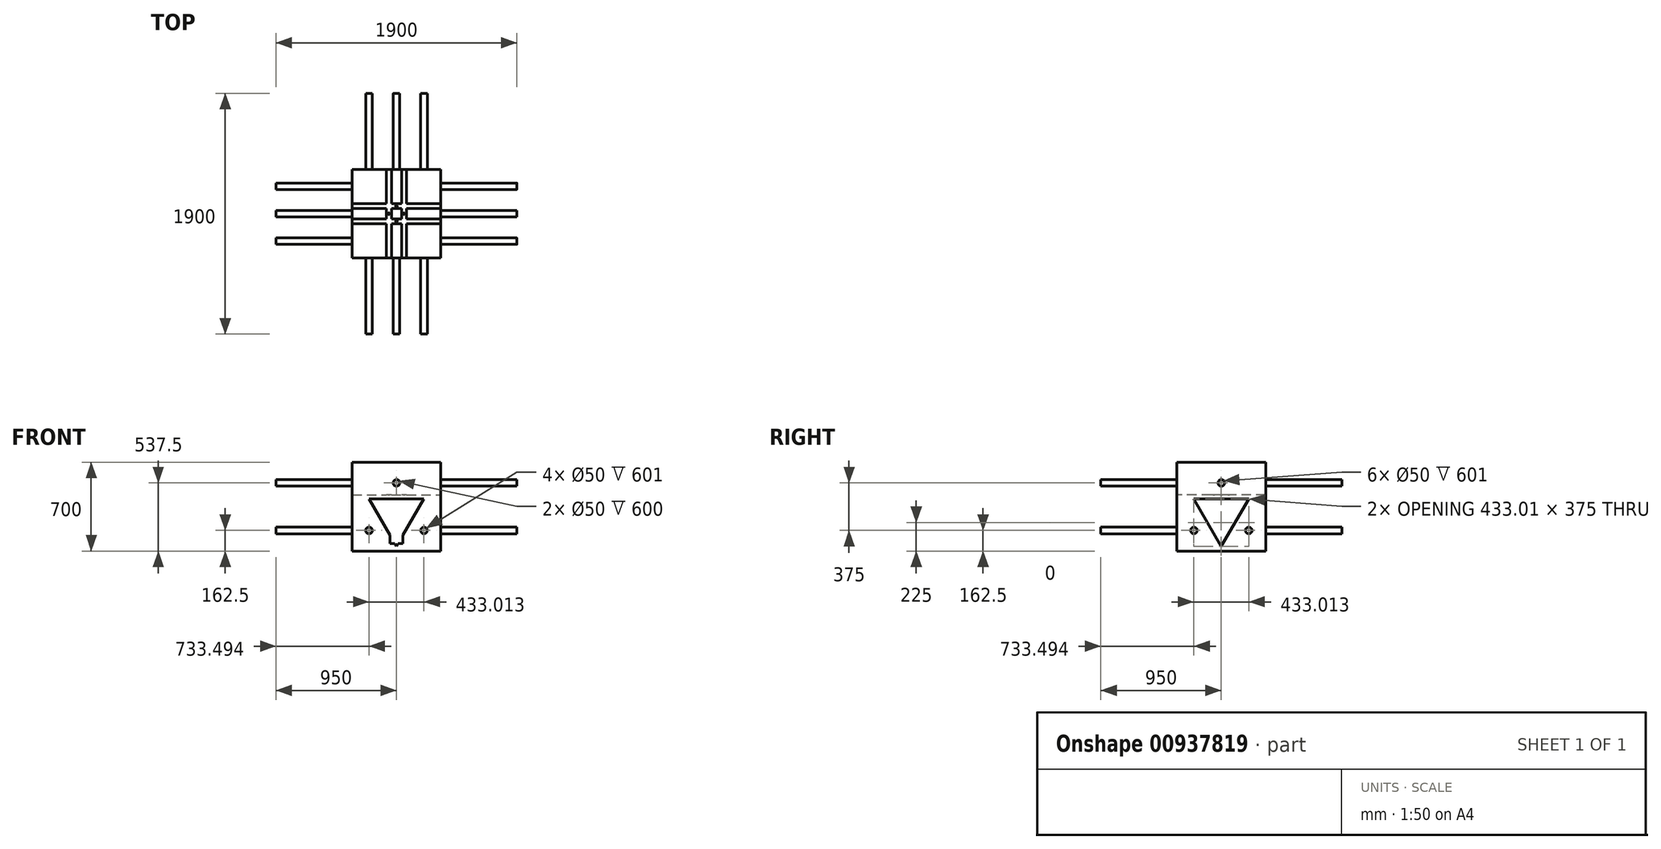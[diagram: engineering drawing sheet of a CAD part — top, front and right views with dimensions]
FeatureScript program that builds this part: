
annotation { "Feature Type Name" : "Feature", "Feature Type Description" : "" }
export const myFeature = defineFeature(function(context is Context, id is Id, definition is map)
    precondition{}
    {
        {
            var Q0;
            Q0=qCreatedBy(makeId("Top.planeOp"),FACE);
            var sketch = newSketch(context, id + "F0", { "sketchPlane" : qUnion([Q0])});
            skLineSegment(sketch, "E0.bottom", {"start": v(350, 350) * mm, "end": v(-350, 350) * mm});
            skLineSegment(sketch, "E0.top", {"start": v(350, -350) * mm, "end": v(-350, -350) * mm});
            skLineSegment(sketch, "E0.left", {"start": v(350, 350) * mm, "end": v(350, -350) * mm});
            skLineSegment(sketch, "E0.right", {"start": v(-350, 350) * mm, "end": v(-350, -350) * mm});
            skPoint(sketch, "E0.middle", {"position": v(0, 0) * mm});
            skLineSegment(sketch, "E1.bottom", {"start": v(349, 349) * mm, "end": v(-349, 349) * mm});
            skLineSegment(sketch, "E1.top", {"start": v(349, -349) * mm, "end": v(-349, -349) * mm});
            skLineSegment(sketch, "E1.left", {"start": v(349, 349) * mm, "end": v(349, -349) * mm});
            skLineSegment(sketch, "E1.right", {"start": v(-349, 349) * mm, "end": v(-349, -349) * mm});
            skLineSegment(sketch, "E2.bottom", {"start": v(-70, 70) * mm, "end": v(70, 70) * mm});
            skLineSegment(sketch, "E2.top", {"start": v(-70, -70) * mm, "end": v(70, -70) * mm});
            skLineSegment(sketch, "E2.left", {"start": v(-70, 70) * mm, "end": v(-70, -70) * mm});
            skLineSegment(sketch, "E2.right", {"start": v(70, 70) * mm, "end": v(70, -70) * mm});
            skSolve(sketch);
        }
        {
            var Q0;
            Q0=makeQuery(id+"F0.imprint","IMPRINT",FACE,{"disambiguationData":[TD([[makeQuery(id+"F0.imprint","IMPRINT",EDGE,{"derivedFrom":sQuery(id+"F0.wireOp",EDGE,"E0.bottom")}),1.0]])]});
            extrude(context, id + "F1", {"entities" : qUnion([Q0]), "oppositeDirection" : true, "depth" : 700 * mm, "offsetDistance" : 25 * mm});
        }
        {
            var Q0;
            Q0=makeQuery(id+"F1.opExtrude","SWEPT_FACE",FACE,{"disambiguationData":[OSD([sQuery(id+"F0.wireOp",EDGE,"E0.left")])]});
            var sketch = newSketch(context, id + "F2", { "sketchPlane" : qUnion([Q0])});
            skPoint(sketch, "E3", {"position": v(0, -350) * mm});
            skPoint(sketch, "E3.positionSnap0", {"position": v(-350, -350) * mm});
            skPoint(sketch, "E3.positionSnap1", {"position": v(0, 0) * mm});
            skCircle(sketch, "E4.cCircle", {"center": v(0, -412.5) * mm, "radius": 250 * mm, "construction": true});
            skLineSegment(sketch, "E4.0", {"start": v(0, -162.5) * mm, "end": v(216.5, -537.5) * mm});
            skLineSegment(sketch, "E4.1", {"start": v(216.5, -537.5) * mm, "end": v(-216.5, -537.5) * mm});
            skLineSegment(sketch, "E4.2", {"start": v(-216.5, -537.5) * mm, "end": v(0, -162.5) * mm});
            skCircle(sketch, "E5", {"center": v(0, -162.5) * mm, "radius": 25 * mm});
            skCircle(sketch, "E6", {"center": v(216.5, -537.5) * mm, "radius": 25 * mm});
            skCircle(sketch, "E7", {"center": v(-216.5, -537.5) * mm, "radius": 25 * mm});
            skCircle(sketch, "E8", {"center": v(0, -162.5) * mm, "radius": 26 * mm});
            skCircle(sketch, "E9", {"center": v(-216.5, -537.5) * mm, "radius": 26 * mm});
            skCircle(sketch, "E10", {"center": v(216.5, -537.5) * mm, "radius": 26 * mm});
            skPoint(sketch, "E11", {"position": v(-350, -175) * mm});
            skPoint(sketch, "E12", {"position": v(350, -175) * mm});
            skLineSegment(sketch, "E13", {"start": v(0, 0) * mm, "end": v(349, -175) * mm});
            skLineSegment(sketch, "E14", {"start": v(349, -175) * mm, "end": v(349, 0) * mm});
            skLineSegment(sketch, "E15", {"start": v(0, 0) * mm, "end": v(-349, -175) * mm});
            skLineSegment(sketch, "E16", {"start": v(-349, -175) * mm, "end": v(-349, 0) * mm});
            skPoint(sketch, "E17.cCircle.perimeterSnap0", {"position": v(0, -537.5) * mm});
            skPoint(sketch, "E17.0.startSnap0", {"position": v(0, -537.5) * mm});
            skLineSegment(sketch, "E18.0", {"start": v(0, -662.5) * mm, "end": v(-216.5, -287.5) * mm});
            skLineSegment(sketch, "E18.1", {"start": v(-216.5, -287.5) * mm, "end": v(216.5, -287.5) * mm});
            skLineSegment(sketch, "E18.2", {"start": v(216.5, -287.5) * mm, "end": v(0, -662.5) * mm});
            skLineSegment(sketch, "E19", {"start": v(-350, -256.5) * mm, "end": v(350, -256.5) * mm});
            skLineSegment(sketch, "E20", {"start": v(-350, -257.5) * mm, "end": v(350, -257.5) * mm});
            skPoint(sketch, "E21", {"position": v(0, -256.5) * mm});
            skPoint(sketch, "E22", {"position": v(0, -257.5) * mm});
            skPoint(sketch, "E23", {"position": v(-80, -256.5) * mm});
            skPoint(sketch, "E24", {"position": v(-80, -257.5) * mm});
            skPoint(sketch, "E25", {"position": v(80, -256.5) * mm});
            skPoint(sketch, "E26", {"position": v(80, -257.5) * mm});
            skLineSegment(sketch, "E27", {"start": v(-80, -256.5) * mm, "end": v(-80, -257.5) * mm});
            skLineSegment(sketch, "E28", {"start": v(80, -256.5) * mm, "end": v(80, -257.5) * mm});
            skPoint(sketch, "E29", {"position": v(-40, -256.5) * mm});
            skPoint(sketch, "E30", {"position": v(-40, -257.5) * mm});
            skPoint(sketch, "E31", {"position": v(40, -256.5) * mm});
            skPoint(sketch, "E32", {"position": v(40, -257.5) * mm});
            skLineSegment(sketch, "E33", {"start": v(-40, -256.5) * mm, "end": v(-40, -257.5) * mm});
            skLineSegment(sketch, "E34", {"start": v(40, -256.5) * mm, "end": v(40, -257.5) * mm});
            skSolve(sketch);
        }
        {
            var Q0;
            Q0=makeQuery(id+"F1.opExtrude","SWEPT_FACE",FACE,{"disambiguationData":[OSD([sQuery(id+"F0.wireOp",EDGE,"E0.top")])]});
            var sketch = newSketch(context, id + "F3", { "sketchPlane" : qUnion([Q0])});
            skPoint(sketch, "E35", {"position": v(0, -412.5) * mm});
            skPoint(sketch, "E35.positionSnap1", {"position": v(0, 157.53) * mm});
            skCircle(sketch, "E36.cCircle", {"center": v(0, -412.5) * mm, "radius": 250 * mm, "construction": true});
            skLineSegment(sketch, "E36.0", {"start": v(0, -162.5) * mm, "end": v(216.5, -537.5) * mm});
            skLineSegment(sketch, "E36.1", {"start": v(216.5, -537.5) * mm, "end": v(-216.5, -537.5) * mm});
            skLineSegment(sketch, "E36.2", {"start": v(-216.5, -537.5) * mm, "end": v(0, -162.5) * mm});
            skCircle(sketch, "E37", {"center": v(0, -162.5) * mm, "radius": 25 * mm});
            skCircle(sketch, "E38", {"center": v(216.5, -537.5) * mm, "radius": 25 * mm});
            skCircle(sketch, "E39", {"center": v(-216.5, -537.5) * mm, "radius": 25 * mm});
            skCircle(sketch, "E40", {"center": v(0, -162.5) * mm, "radius": 26 * mm});
            skCircle(sketch, "E41", {"center": v(-216.5, -537.5) * mm, "radius": 26 * mm});
            skCircle(sketch, "E42", {"center": v(216.5, -537.5) * mm, "radius": 26 * mm});
            skPoint(sketch, "E43", {"position": v(-350, -350) * mm});
            skPoint(sketch, "E44", {"position": v(-350, -175) * mm});
            skPoint(sketch, "E45", {"position": v(350, -175) * mm});
            skLineSegment(sketch, "E46", {"start": v(0, 0) * mm, "end": v(-349, -175) * mm});
            skLineSegment(sketch, "E47", {"start": v(-349, -175) * mm, "end": v(-349, 0) * mm});
            skLineSegment(sketch, "E48", {"start": v(0, 0) * mm, "end": v(349, -175) * mm});
            skLineSegment(sketch, "E49", {"start": v(349, -175) * mm, "end": v(349, 0) * mm});
            skLineSegment(sketch, "E50.0", {"start": v(0, -662.5) * mm, "end": v(-216.5, -287.5) * mm});
            skLineSegment(sketch, "E50.1", {"start": v(-216.5, -287.5) * mm, "end": v(216.5, -287.5) * mm});
            skLineSegment(sketch, "E50.2", {"start": v(216.5, -287.5) * mm, "end": v(0, -662.5) * mm});
            skPoint(sketch, "E51", {"position": v(-350, -257.5) * mm});
            skPoint(sketch, "E52", {"position": v(-350, -256.5) * mm});
            skPoint(sketch, "E53", {"position": v(350, -256.5) * mm});
            skPoint(sketch, "E54", {"position": v(350, -257.5) * mm});
            skLineSegment(sketch, "E55", {"start": v(-350, -256.5) * mm, "end": v(350, -256.5) * mm});
            skLineSegment(sketch, "E56", {"start": v(-350, -257.5) * mm, "end": v(350, -257.5) * mm});
            skPoint(sketch, "E57", {"position": v(0, -257.5) * mm});
            skPoint(sketch, "E58", {"position": v(0, -256.5) * mm});
            skPoint(sketch, "E59", {"position": v(-80, -256.5) * mm});
            skPoint(sketch, "E60", {"position": v(-80, -257.5) * mm});
            skPoint(sketch, "E61", {"position": v(80, -256.5) * mm});
            skPoint(sketch, "E62", {"position": v(80, -257.5) * mm});
            skPoint(sketch, "E63", {"position": v(-40, -256.5) * mm});
            skPoint(sketch, "E64", {"position": v(-40, -257.5) * mm});
            skPoint(sketch, "E65", {"position": v(40, -256.5) * mm});
            skPoint(sketch, "E66", {"position": v(40, -257.5) * mm});
            skLineSegment(sketch, "E67", {"start": v(-80, -256.5) * mm, "end": v(-80, -257.5) * mm});
            skLineSegment(sketch, "E68", {"start": v(-40, -256.5) * mm, "end": v(-40, -257.5) * mm});
            skLineSegment(sketch, "E69", {"start": v(40, -256.5) * mm, "end": v(40, -257.5) * mm});
            skLineSegment(sketch, "E70", {"start": v(80, -257.5) * mm, "end": v(80, -256.5) * mm});
            skSolve(sketch);
        }
        {
            var Q0;
            Q0=makeQuery(id+"F1.opExtrude","SWEPT_FACE",FACE,{"disambiguationData":[OSD([sQuery(id+"F0.wireOp",EDGE,"E0.right")])]});
            var sketch = newSketch(context, id + "F4", { "sketchPlane" : qUnion([Q0])});
            skPoint(sketch, "E71", {"position": v(0, -350) * mm});
            skPoint(sketch, "E71.positionSnap0", {"position": v(-350, -350) * mm});
            skPoint(sketch, "E71.positionSnap1", {"position": v(0, 0) * mm});
            skCircle(sketch, "E72.cCircle", {"center": v(0, -412.5) * mm, "radius": 250 * mm, "construction": true});
            skLineSegment(sketch, "E72.0", {"start": v(0, -162.5) * mm, "end": v(216.5, -537.5) * mm});
            skLineSegment(sketch, "E72.1", {"start": v(216.5, -537.5) * mm, "end": v(-216.5, -537.5) * mm});
            skLineSegment(sketch, "E72.2", {"start": v(-216.5, -537.5) * mm, "end": v(0, -162.5) * mm});
            skCircle(sketch, "E73", {"center": v(0, -162.5) * mm, "radius": 25 * mm});
            skCircle(sketch, "E74", {"center": v(216.5, -537.5) * mm, "radius": 25 * mm});
            skCircle(sketch, "E75", {"center": v(-216.5, -537.5) * mm, "radius": 25 * mm});
            skCircle(sketch, "E76", {"center": v(0, -162.5) * mm, "radius": 26 * mm});
            skCircle(sketch, "E77", {"center": v(-216.5, -537.5) * mm, "radius": 26 * mm});
            skCircle(sketch, "E78", {"center": v(216.5, -537.5) * mm, "radius": 26 * mm});
            skSolve(sketch);
        }
        {
            var Q0;
            Q0=makeQuery(id+"F1.opExtrude","SWEPT_FACE",FACE,{"disambiguationData":[OSD([sQuery(id+"F0.wireOp",EDGE,"E0.bottom")])]});
            var sketch = newSketch(context, id + "F5", { "sketchPlane" : qUnion([Q0])});
            skPoint(sketch, "E79", {"position": v(0, -350) * mm});
            skPoint(sketch, "E79.positionSnap0", {"position": v(-350, -350) * mm});
            skPoint(sketch, "E79.positionSnap1", {"position": v(0, 0) * mm});
            skCircle(sketch, "E80.cCircle", {"center": v(0, -412.5) * mm, "radius": 250 * mm, "construction": true});
            skLineSegment(sketch, "E80.0", {"start": v(0, -162.5) * mm, "end": v(216.5, -537.5) * mm});
            skLineSegment(sketch, "E80.1", {"start": v(216.5, -537.5) * mm, "end": v(-216.5, -537.5) * mm});
            skLineSegment(sketch, "E80.2", {"start": v(-216.5, -537.5) * mm, "end": v(0, -162.5) * mm});
            skCircle(sketch, "E81", {"center": v(0, -162.5) * mm, "radius": 25 * mm});
            skCircle(sketch, "E82", {"center": v(216.5, -537.5) * mm, "radius": 25 * mm});
            skCircle(sketch, "E83", {"center": v(-216.5, -537.5) * mm, "radius": 25 * mm});
            skCircle(sketch, "E84", {"center": v(0, -162.5) * mm, "radius": 26 * mm});
            skCircle(sketch, "E85", {"center": v(216.5, -537.5) * mm, "radius": 26 * mm});
            skCircle(sketch, "E86", {"center": v(-216.5, -537.5) * mm, "radius": 26 * mm});
            skSolve(sketch);
        }
        {
            var Q0;
            {var subQ0=sQuery(id+"F2.wireOp",EDGE,"E5");var subQ1=sQuery(id+"F2.wireOp",EDGE,"E4.0");var subQ2=makeQuery(id+"F2.imprint","INTERSECT",VERTEX,{"derivedFrom":[subQ1,subQ0]});Q0=makeQuery(id+"F2.imprint","IMPRINT",FACE,{"disambiguationData":[TD([[makeQuery(id+"F2.imprint","IMPRINT",EDGE,{"disambiguationData":[TD([[subQ2,-1.0]])],"derivedFrom":subQ1}),1.0]])]});}
            var Q1;
            {var subQ0=sQuery(id+"F2.wireOp",EDGE,"E10");var subQ1=sQuery(id+"F2.wireOp",EDGE,"E4.0");var subQ2=makeQuery(id+"F2.imprint","INTERSECT",VERTEX,{"derivedFrom":[subQ1,subQ0]});Q1=makeQuery(id+"F2.imprint","IMPRINT",FACE,{"disambiguationData":[TD([[makeQuery(id+"F2.imprint","IMPRINT",EDGE,{"disambiguationData":[TD([[subQ2,-1.0]])],"derivedFrom":subQ1}),1.0]])]});}
            var Q2;
            {var subQ0=sQuery(id+"F2.wireOp",EDGE,"E10");var subQ1=sQuery(id+"F2.wireOp",EDGE,"E4.0");var subQ2=makeQuery(id+"F2.imprint","INTERSECT",VERTEX,{"derivedFrom":[subQ1,subQ0]});Q2=makeQuery(id+"F2.imprint","IMPRINT",FACE,{"disambiguationData":[TD([[makeQuery(id+"F2.imprint","IMPRINT",EDGE,{"disambiguationData":[TD([[subQ2,-1.0]])],"derivedFrom":subQ1}),-1.0]])]});}
            var Q3;
            {var subQ0=sQuery(id+"F2.wireOp",EDGE,"E5");var subQ1=sQuery(id+"F2.wireOp",EDGE,"E4.0");var subQ2=makeQuery(id+"F2.imprint","INTERSECT",VERTEX,{"derivedFrom":[subQ1,subQ0]});Q3=makeQuery(id+"F2.imprint","IMPRINT",FACE,{"disambiguationData":[TD([[makeQuery(id+"F2.imprint","IMPRINT",EDGE,{"disambiguationData":[TD([[subQ2,-1.0]])],"derivedFrom":subQ1}),-1.0]])]});}
            var Q4;
            {var subQ0=sQuery(id+"F2.wireOp",EDGE,"E9");var subQ1=sQuery(id+"F2.wireOp",EDGE,"E4.1");var subQ2=makeQuery(id+"F2.imprint","INTERSECT",VERTEX,{"derivedFrom":[subQ1,subQ0]});Q4=makeQuery(id+"F2.imprint","IMPRINT",FACE,{"disambiguationData":[TD([[makeQuery(id+"F2.imprint","IMPRINT",EDGE,{"disambiguationData":[TD([[subQ2,-1.0]])],"derivedFrom":subQ1}),1.0]])]});}
            var Q5;
            {var subQ0=sQuery(id+"F2.wireOp",EDGE,"E9");var subQ1=sQuery(id+"F2.wireOp",EDGE,"E4.1");var subQ2=makeQuery(id+"F2.imprint","INTERSECT",VERTEX,{"derivedFrom":[subQ1,subQ0]});Q5=makeQuery(id+"F2.imprint","IMPRINT",FACE,{"disambiguationData":[TD([[makeQuery(id+"F2.imprint","IMPRINT",EDGE,{"disambiguationData":[TD([[subQ2,-1.0]])],"derivedFrom":subQ1}),-1.0]])]});}
            extrude(context, id + "F6", {"entities" : qUnion([Q0, Q1, Q2, Q3, Q4, Q5]), "operationType" : NewBodyOperationType.ADD, "depth" : 600 * mm, "offsetDistance" : 25 * mm});
        }
        {
            var Q0;
            {var subQ0=sQuery(id+"F3.wireOp",EDGE,"E37");var subQ1=sQuery(id+"F3.wireOp",EDGE,"E36.0");var subQ2=makeQuery(id+"F3.imprint","INTERSECT",VERTEX,{"derivedFrom":[subQ1,subQ0]});Q0=makeQuery(id+"F3.imprint","IMPRINT",FACE,{"disambiguationData":[TD([[makeQuery(id+"F3.imprint","IMPRINT",EDGE,{"disambiguationData":[TD([[subQ2,-1.0]])],"derivedFrom":subQ1}),-1.0]])]});}
            var Q1;
            {var subQ0=sQuery(id+"F3.wireOp",EDGE,"E37");var subQ1=sQuery(id+"F3.wireOp",EDGE,"E36.0");var subQ2=makeQuery(id+"F3.imprint","INTERSECT",VERTEX,{"derivedFrom":[subQ1,subQ0]});Q1=makeQuery(id+"F3.imprint","IMPRINT",FACE,{"disambiguationData":[TD([[makeQuery(id+"F3.imprint","IMPRINT",EDGE,{"disambiguationData":[TD([[subQ2,-1.0]])],"derivedFrom":subQ1}),1.0]])]});}
            var Q2;
            {var subQ0=sQuery(id+"F3.wireOp",EDGE,"E41");var subQ1=sQuery(id+"F3.wireOp",EDGE,"E36.1");var subQ2=makeQuery(id+"F3.imprint","INTERSECT",VERTEX,{"derivedFrom":[subQ1,subQ0]});Q2=makeQuery(id+"F3.imprint","IMPRINT",FACE,{"disambiguationData":[TD([[makeQuery(id+"F3.imprint","IMPRINT",EDGE,{"disambiguationData":[TD([[subQ2,-1.0]])],"derivedFrom":subQ1}),1.0]])]});}
            var Q3;
            {var subQ0=sQuery(id+"F3.wireOp",EDGE,"E41");var subQ1=sQuery(id+"F3.wireOp",EDGE,"E36.1");var subQ2=makeQuery(id+"F3.imprint","INTERSECT",VERTEX,{"derivedFrom":[subQ1,subQ0]});Q3=makeQuery(id+"F3.imprint","IMPRINT",FACE,{"disambiguationData":[TD([[makeQuery(id+"F3.imprint","IMPRINT",EDGE,{"disambiguationData":[TD([[subQ2,-1.0]])],"derivedFrom":subQ1}),-1.0]])]});}
            var Q4;
            {var subQ0=sQuery(id+"F3.wireOp",EDGE,"E42");var subQ1=sQuery(id+"F3.wireOp",EDGE,"E36.0");var subQ2=makeQuery(id+"F3.imprint","INTERSECT",VERTEX,{"derivedFrom":[subQ1,subQ0]});Q4=makeQuery(id+"F3.imprint","IMPRINT",FACE,{"disambiguationData":[TD([[makeQuery(id+"F3.imprint","IMPRINT",EDGE,{"disambiguationData":[TD([[subQ2,-1.0]])],"derivedFrom":subQ1}),1.0]])]});}
            var Q5;
            {var subQ0=sQuery(id+"F3.wireOp",EDGE,"E42");var subQ1=sQuery(id+"F3.wireOp",EDGE,"E36.0");var subQ2=makeQuery(id+"F3.imprint","INTERSECT",VERTEX,{"derivedFrom":[subQ1,subQ0]});Q5=makeQuery(id+"F3.imprint","IMPRINT",FACE,{"disambiguationData":[TD([[makeQuery(id+"F3.imprint","IMPRINT",EDGE,{"disambiguationData":[TD([[subQ2,-1.0]])],"derivedFrom":subQ1}),-1.0]])]});}
            extrude(context, id + "F7", {"entities" : qUnion([Q0, Q1, Q2, Q3, Q4, Q5]), "operationType" : NewBodyOperationType.ADD, "depth" : 600 * mm, "offsetDistance" : 25 * mm});
        }
        {
            var Q0;
            {var subQ0=sQuery(id+"F4.wireOp",EDGE,"E73");var subQ1=sQuery(id+"F4.wireOp",EDGE,"E72.0");var subQ2=makeQuery(id+"F4.imprint","INTERSECT",VERTEX,{"derivedFrom":[subQ1,subQ0]});Q0=makeQuery(id+"F4.imprint","IMPRINT",FACE,{"disambiguationData":[TD([[makeQuery(id+"F4.imprint","IMPRINT",EDGE,{"disambiguationData":[TD([[subQ2,-1.0]])],"derivedFrom":subQ1}),1.0]])]});}
            var Q1;
            {var subQ0=sQuery(id+"F4.wireOp",EDGE,"E73");var subQ1=sQuery(id+"F4.wireOp",EDGE,"E72.0");var subQ2=makeQuery(id+"F4.imprint","INTERSECT",VERTEX,{"derivedFrom":[subQ1,subQ0]});Q1=makeQuery(id+"F4.imprint","IMPRINT",FACE,{"disambiguationData":[TD([[makeQuery(id+"F4.imprint","IMPRINT",EDGE,{"disambiguationData":[TD([[subQ2,-1.0]])],"derivedFrom":subQ1}),-1.0]])]});}
            var Q2;
            {var subQ0=sQuery(id+"F4.wireOp",EDGE,"E78");var subQ1=sQuery(id+"F4.wireOp",EDGE,"E72.0");var subQ2=makeQuery(id+"F4.imprint","INTERSECT",VERTEX,{"derivedFrom":[subQ1,subQ0]});Q2=makeQuery(id+"F4.imprint","IMPRINT",FACE,{"disambiguationData":[TD([[makeQuery(id+"F4.imprint","IMPRINT",EDGE,{"disambiguationData":[TD([[subQ2,-1.0]])],"derivedFrom":subQ1}),1.0]])]});}
            var Q3;
            {var subQ0=sQuery(id+"F4.wireOp",EDGE,"E78");var subQ1=sQuery(id+"F4.wireOp",EDGE,"E72.0");var subQ2=makeQuery(id+"F4.imprint","INTERSECT",VERTEX,{"derivedFrom":[subQ1,subQ0]});Q3=makeQuery(id+"F4.imprint","IMPRINT",FACE,{"disambiguationData":[TD([[makeQuery(id+"F4.imprint","IMPRINT",EDGE,{"disambiguationData":[TD([[subQ2,-1.0]])],"derivedFrom":subQ1}),-1.0]])]});}
            var Q4;
            {var subQ0=sQuery(id+"F4.wireOp",EDGE,"E77");var subQ1=sQuery(id+"F4.wireOp",EDGE,"E72.1");var subQ2=makeQuery(id+"F4.imprint","INTERSECT",VERTEX,{"derivedFrom":[subQ1,subQ0]});Q4=makeQuery(id+"F4.imprint","IMPRINT",FACE,{"disambiguationData":[TD([[makeQuery(id+"F4.imprint","IMPRINT",EDGE,{"disambiguationData":[TD([[subQ2,-1.0]])],"derivedFrom":subQ1}),1.0]])]});}
            var Q5;
            {var subQ0=sQuery(id+"F4.wireOp",EDGE,"E77");var subQ1=sQuery(id+"F4.wireOp",EDGE,"E72.1");var subQ2=makeQuery(id+"F4.imprint","INTERSECT",VERTEX,{"derivedFrom":[subQ1,subQ0]});Q5=makeQuery(id+"F4.imprint","IMPRINT",FACE,{"disambiguationData":[TD([[makeQuery(id+"F4.imprint","IMPRINT",EDGE,{"disambiguationData":[TD([[subQ2,-1.0]])],"derivedFrom":subQ1}),-1.0]])]});}
            extrude(context, id + "F8", {"entities" : qUnion([Q0, Q1, Q2, Q3, Q4, Q5]), "operationType" : NewBodyOperationType.ADD, "depth" : 600 * mm, "offsetDistance" : 25 * mm});
        }
        {
            var Q0;
            {var subQ0=sQuery(id+"F5.wireOp",EDGE,"E81");var subQ1=sQuery(id+"F5.wireOp",EDGE,"E80.0");var subQ2=makeQuery(id+"F5.imprint","INTERSECT",VERTEX,{"derivedFrom":[subQ1,subQ0]});Q0=makeQuery(id+"F5.imprint","IMPRINT",FACE,{"disambiguationData":[TD([[makeQuery(id+"F5.imprint","IMPRINT",EDGE,{"disambiguationData":[TD([[subQ2,-1.0]])],"derivedFrom":subQ1}),-1.0]])]});}
            var Q1;
            {var subQ0=sQuery(id+"F5.wireOp",EDGE,"E81");var subQ1=sQuery(id+"F5.wireOp",EDGE,"E80.0");var subQ2=makeQuery(id+"F5.imprint","INTERSECT",VERTEX,{"derivedFrom":[subQ1,subQ0]});Q1=makeQuery(id+"F5.imprint","IMPRINT",FACE,{"disambiguationData":[TD([[makeQuery(id+"F5.imprint","IMPRINT",EDGE,{"disambiguationData":[TD([[subQ2,-1.0]])],"derivedFrom":subQ1}),1.0]])]});}
            var Q2;
            {var subQ0=sQuery(id+"F5.wireOp",EDGE,"E86");var subQ1=sQuery(id+"F5.wireOp",EDGE,"E80.1");var subQ2=makeQuery(id+"F5.imprint","INTERSECT",VERTEX,{"derivedFrom":[subQ1,subQ0]});Q2=makeQuery(id+"F5.imprint","IMPRINT",FACE,{"disambiguationData":[TD([[makeQuery(id+"F5.imprint","IMPRINT",EDGE,{"disambiguationData":[TD([[subQ2,-1.0]])],"derivedFrom":subQ1}),1.0]])]});}
            var Q3;
            {var subQ0=sQuery(id+"F5.wireOp",EDGE,"E86");var subQ1=sQuery(id+"F5.wireOp",EDGE,"E80.1");var subQ2=makeQuery(id+"F5.imprint","INTERSECT",VERTEX,{"derivedFrom":[subQ1,subQ0]});Q3=makeQuery(id+"F5.imprint","IMPRINT",FACE,{"disambiguationData":[TD([[makeQuery(id+"F5.imprint","IMPRINT",EDGE,{"disambiguationData":[TD([[subQ2,-1.0]])],"derivedFrom":subQ1}),-1.0]])]});}
            var Q4;
            {var subQ0=sQuery(id+"F5.wireOp",EDGE,"E85");var subQ1=sQuery(id+"F5.wireOp",EDGE,"E80.0");var subQ2=makeQuery(id+"F5.imprint","INTERSECT",VERTEX,{"derivedFrom":[subQ1,subQ0]});Q4=makeQuery(id+"F5.imprint","IMPRINT",FACE,{"disambiguationData":[TD([[makeQuery(id+"F5.imprint","IMPRINT",EDGE,{"disambiguationData":[TD([[subQ2,-1.0]])],"derivedFrom":subQ1}),-1.0]])]});}
            var Q5;
            {var subQ0=sQuery(id+"F5.wireOp",EDGE,"E85");var subQ1=sQuery(id+"F5.wireOp",EDGE,"E80.0");var subQ2=makeQuery(id+"F5.imprint","INTERSECT",VERTEX,{"derivedFrom":[subQ1,subQ0]});Q5=makeQuery(id+"F5.imprint","IMPRINT",FACE,{"disambiguationData":[TD([[makeQuery(id+"F5.imprint","IMPRINT",EDGE,{"disambiguationData":[TD([[subQ2,-1.0]])],"derivedFrom":subQ1}),1.0]])]});}
            extrude(context, id + "F9", {"entities" : qUnion([Q0, Q1, Q2, Q3, Q4, Q5]), "operationType" : NewBodyOperationType.ADD, "depth" : 600 * mm, "offsetDistance" : 25 * mm});
        }
        {
            var Q0;
            Q0=makeQuery(id+"F6.boolean.opBoolean","SPLIT",FACE,{"disambiguationData":[TD([makeQuery(id+"F6.opExtrude","SWEPT_FACE",FACE,{"disambiguationData":[OSD([sQuery(id+"F2.wireOp",EDGE,"E7")])]})])],"derivedFrom":makeQuery(id+"F1.opExtrude","SWEPT_FACE",FACE,{"disambiguationData":[OSD([sQuery(id+"F0.wireOp",EDGE,"E0.left")])]})});
            extrude(context, id + "F10", {"entities" : qUnion([Q0]), "operationType" : NewBodyOperationType.REMOVE, "oppositeDirection" : true, "depth" : 25 * mm, "offsetDistance" : 25 * mm});
        }
        {
            var Q0;
            Q0=makeQuery(id+"F6.boolean.opBoolean","SPLIT",FACE,{"disambiguationData":[TD([makeQuery(id+"F6.opExtrude","SWEPT_FACE",FACE,{"disambiguationData":[OSD([sQuery(id+"F2.wireOp",EDGE,"E6")])]})])],"derivedFrom":makeQuery(id+"F1.opExtrude","SWEPT_FACE",FACE,{"disambiguationData":[OSD([sQuery(id+"F0.wireOp",EDGE,"E0.left")])]})});
            extrude(context, id + "F11", {"entities" : qUnion([Q0]), "operationType" : NewBodyOperationType.REMOVE, "oppositeDirection" : true, "depth" : 25 * mm, "offsetDistance" : 25 * mm});
        }
        {
            var Q0;
            Q0=makeQuery(id+"F8.boolean.opBoolean","SPLIT",FACE,{"disambiguationData":[TD([makeQuery(id+"F8.opExtrude","SWEPT_FACE",FACE,{"disambiguationData":[OSD([sQuery(id+"F4.wireOp",EDGE,"E75")])]})])],"derivedFrom":makeQuery(id+"F1.opExtrude","SWEPT_FACE",FACE,{"disambiguationData":[OSD([sQuery(id+"F0.wireOp",EDGE,"E0.right")])]})});
            extrude(context, id + "F12", {"entities" : qUnion([Q0]), "operationType" : NewBodyOperationType.REMOVE, "oppositeDirection" : true, "depth" : 25 * mm, "offsetDistance" : 25 * mm});
        }
        {
            var Q0;
            Q0=makeQuery(id+"F8.boolean.opBoolean","SPLIT",FACE,{"disambiguationData":[TD([makeQuery(id+"F8.opExtrude","SWEPT_FACE",FACE,{"disambiguationData":[OSD([sQuery(id+"F4.wireOp",EDGE,"E74")])]})])],"derivedFrom":makeQuery(id+"F1.opExtrude","SWEPT_FACE",FACE,{"disambiguationData":[OSD([sQuery(id+"F0.wireOp",EDGE,"E0.right")])]})});
            extrude(context, id + "F13", {"entities" : qUnion([Q0]), "operationType" : NewBodyOperationType.REMOVE, "oppositeDirection" : true, "depth" : 25 * mm, "offsetDistance" : 25 * mm});
        }
        {
            var Q0;
            Q0=makeQuery(id+"F9.boolean.opBoolean","SPLIT",FACE,{"disambiguationData":[TD([makeQuery(id+"F9.opExtrude","SWEPT_FACE",FACE,{"disambiguationData":[OSD([sQuery(id+"F5.wireOp",EDGE,"E82")])]})])],"derivedFrom":makeQuery(id+"F1.opExtrude","SWEPT_FACE",FACE,{"disambiguationData":[OSD([sQuery(id+"F0.wireOp",EDGE,"E0.bottom")])]})});
            var Q1;
            Q1=makeQuery(id+"F9.boolean.opBoolean","SPLIT",FACE,{"disambiguationData":[TD([makeQuery(id+"F9.opExtrude","SWEPT_FACE",FACE,{"disambiguationData":[OSD([sQuery(id+"F5.wireOp",EDGE,"E83")])]})])],"derivedFrom":makeQuery(id+"F1.opExtrude","SWEPT_FACE",FACE,{"disambiguationData":[OSD([sQuery(id+"F0.wireOp",EDGE,"E0.bottom")])]})});
            extrude(context, id + "F14", {"entities" : qUnion([Q0, Q1]), "operationType" : NewBodyOperationType.REMOVE, "oppositeDirection" : true, "depth" : 25 * mm, "offsetDistance" : 25 * mm});
        }
        {
            var Q0;
            Q0=makeQuery(id+"F7.boolean.opBoolean","SPLIT",FACE,{"disambiguationData":[TD([makeQuery(id+"F7.opExtrude","SWEPT_FACE",FACE,{"disambiguationData":[OSD([sQuery(id+"F3.wireOp",EDGE,"E38")])]})])],"derivedFrom":makeQuery(id+"F1.opExtrude","SWEPT_FACE",FACE,{"disambiguationData":[OSD([sQuery(id+"F0.wireOp",EDGE,"E0.top")])]})});
            var Q1;
            Q1=makeQuery(id+"F7.boolean.opBoolean","SPLIT",FACE,{"disambiguationData":[TD([makeQuery(id+"F7.opExtrude","SWEPT_FACE",FACE,{"disambiguationData":[OSD([sQuery(id+"F3.wireOp",EDGE,"E39")])]})])],"derivedFrom":makeQuery(id+"F1.opExtrude","SWEPT_FACE",FACE,{"disambiguationData":[OSD([sQuery(id+"F0.wireOp",EDGE,"E0.top")])]})});
            extrude(context, id + "F15", {"entities" : qUnion([Q0, Q1]), "operationType" : NewBodyOperationType.REMOVE, "oppositeDirection" : true, "depth" : 25 * mm, "offsetDistance" : 25 * mm});
        }
        {
            var Q0;
            Q0=makeQuery(id+"F6.boolean.opBoolean","SPLIT",FACE,{"disambiguationData":[TD([makeQuery(id+"F6.opExtrude","SWEPT_FACE",FACE,{"disambiguationData":[OSD([sQuery(id+"F2.wireOp",EDGE,"E5")])]})])],"derivedFrom":makeQuery(id+"F1.opExtrude","SWEPT_FACE",FACE,{"disambiguationData":[OSD([sQuery(id+"F0.wireOp",EDGE,"E0.left")])]})});
            extrude(context, id + "F16", {"entities" : qUnion([Q0]), "operationType" : NewBodyOperationType.REMOVE, "oppositeDirection" : true, "depth" : 4990 * mm, "offsetDistance" : 25 * mm});
        }
        {
            var Q0;
            {var subQ0=sQuery(id+"F2.wireOp",EDGE,"E18.1");var subQ1=sQuery(id+"F2.wireOp",EDGE,"E4.0");var subQ2=makeQuery(id+"F2.imprint","INTERSECT",VERTEX,{"derivedFrom":[subQ1,subQ0]});Q0=makeQuery(id+"F2.imprint","IMPRINT",FACE,{"disambiguationData":[TD([[makeQuery(id+"F2.imprint","IMPRINT",EDGE,{"disambiguationData":[TD([[subQ2,-1.0]])],"derivedFrom":subQ1}),1.0]])]});}
            var Q1;
            {var subQ3=sQuery(id+"F2.wireOp",EDGE,"E18.1");var subQ9=sQuery(id+"F2.wireOp",EDGE,"E4.0");var subQ10=makeQuery(id+"F2.imprint","INTERSECT",VERTEX,{"derivedFrom":[subQ9,subQ3]});Q1=makeQuery(id+"F2.imprint","IMPRINT",FACE,{"disambiguationData":[TD([[makeQuery(id+"F2.imprint","IMPRINT",EDGE,{"disambiguationData":[TD([[subQ10,-1.0]])],"derivedFrom":subQ9}),-1.0]])]});}
            var Q2;
            {var subQ0=sQuery(id+"F2.wireOp",EDGE,"E18.0");var subQ1=sQuery(id+"F2.wireOp",EDGE,"E4.2");var subQ2=makeQuery(id+"F2.imprint","INTERSECT",VERTEX,{"derivedFrom":[subQ1,subQ0]});Q2=makeQuery(id+"F2.imprint","IMPRINT",FACE,{"disambiguationData":[TD([[makeQuery(id+"F2.imprint","IMPRINT",EDGE,{"disambiguationData":[TD([[subQ2,-1.0]])],"derivedFrom":subQ1}),1.0]])]});}
            var Q3;
            {var subQ0=sQuery(id+"F2.wireOp",EDGE,"E18.2");var subQ1=sQuery(id+"F2.wireOp",EDGE,"E4.1");var subQ2=makeQuery(id+"F2.imprint","INTERSECT",VERTEX,{"derivedFrom":[subQ1,subQ0]});Q3=makeQuery(id+"F2.imprint","IMPRINT",FACE,{"disambiguationData":[TD([[makeQuery(id+"F2.imprint","IMPRINT",EDGE,{"disambiguationData":[TD([[subQ2,-1.0]])],"derivedFrom":subQ1}),1.0]])]});}
            extrude(context, id + "F17", {"entities" : qUnion([Q0, Q1, Q2, Q3]), "operationType" : NewBodyOperationType.REMOVE, "oppositeDirection" : true, "depth" : 700 * mm, "offsetDistance" : 25 * mm});
        }
        {
            var Q0;
            {var subQ0=sQuery(id+"F3.wireOp",EDGE,"E50.0");var subQ1=sQuery(id+"F3.wireOp",EDGE,"E36.2");var subQ2=makeQuery(id+"F3.imprint","INTERSECT",VERTEX,{"derivedFrom":[subQ1,subQ0]});Q0=makeQuery(id+"F3.imprint","IMPRINT",FACE,{"disambiguationData":[TD([[makeQuery(id+"F3.imprint","IMPRINT",EDGE,{"disambiguationData":[TD([[subQ2,-1.0]])],"derivedFrom":subQ1}),1.0]])]});}
            var Q1;
            {var subQ3=sQuery(id+"F3.wireOp",EDGE,"E50.1");var subQ9=sQuery(id+"F3.wireOp",EDGE,"E36.0");var subQ10=makeQuery(id+"F3.imprint","INTERSECT",VERTEX,{"derivedFrom":[subQ9,subQ3]});Q1=makeQuery(id+"F3.imprint","IMPRINT",FACE,{"disambiguationData":[TD([[makeQuery(id+"F3.imprint","IMPRINT",EDGE,{"disambiguationData":[TD([[subQ10,-1.0]])],"derivedFrom":subQ9}),-1.0]])]});}
            var Q2;
            {var subQ0=sQuery(id+"F3.wireOp",EDGE,"E50.1");var subQ1=sQuery(id+"F3.wireOp",EDGE,"E36.0");var subQ2=makeQuery(id+"F3.imprint","INTERSECT",VERTEX,{"derivedFrom":[subQ1,subQ0]});Q2=makeQuery(id+"F3.imprint","IMPRINT",FACE,{"disambiguationData":[TD([[makeQuery(id+"F3.imprint","IMPRINT",EDGE,{"disambiguationData":[TD([[subQ2,-1.0]])],"derivedFrom":subQ1}),1.0]])]});}
            var Q3;
            {var subQ0=sQuery(id+"F3.wireOp",EDGE,"E50.2");var subQ1=sQuery(id+"F3.wireOp",EDGE,"E36.1");var subQ2=makeQuery(id+"F3.imprint","INTERSECT",VERTEX,{"derivedFrom":[subQ1,subQ0]});Q3=makeQuery(id+"F3.imprint","IMPRINT",FACE,{"disambiguationData":[TD([[makeQuery(id+"F3.imprint","IMPRINT",EDGE,{"disambiguationData":[TD([[subQ2,-1.0]])],"derivedFrom":subQ1}),1.0]])]});}
            extrude(context, id + "F18", {"entities" : qUnion([Q0, Q1, Q2, Q3]), "operationType" : NewBodyOperationType.REMOVE, "oppositeDirection" : true, "depth" : 700 * mm, "offsetDistance" : 25 * mm});
        }
        {
            var Q0;
            {var subQ5=sQuery(id+"F2.wireOp",EDGE,"E27");Q0=makeQuery(id+"F2.imprint","IMPRINT",FACE,{"disambiguationData":[TD([[makeQuery(id+"F2.imprint","IMPRINT",EDGE,{"derivedFrom":subQ5}),1.0]])]});}
            var Q1;
            {var subQ5=sQuery(id+"F2.wireOp",EDGE,"E33");Q1=makeQuery(id+"F2.imprint","IMPRINT",FACE,{"disambiguationData":[TD([[makeQuery(id+"F2.imprint","IMPRINT",EDGE,{"derivedFrom":subQ5}),-1.0]])]});}
            var Q2;
            {var subQ5=sQuery(id+"F2.wireOp",EDGE,"E34");Q2=makeQuery(id+"F2.imprint","IMPRINT",FACE,{"disambiguationData":[TD([[makeQuery(id+"F2.imprint","IMPRINT",EDGE,{"derivedFrom":subQ5}),1.0]])]});}
            var Q3;
            {var subQ5=sQuery(id+"F2.wireOp",EDGE,"E28");Q3=makeQuery(id+"F2.imprint","IMPRINT",FACE,{"disambiguationData":[TD([[makeQuery(id+"F2.imprint","IMPRINT",EDGE,{"derivedFrom":subQ5}),-1.0]])]});}
            extrude(context, id + "F19", {"entities" : qUnion([Q0, Q1, Q2, Q3]), "operationType" : NewBodyOperationType.ADD, "oppositeDirection" : true, "depth" : 700 * mm, "offsetDistance" : 25 * mm});
        }
        {
            var Q0;
            {var subQ5=sQuery(id+"F3.wireOp",EDGE,"E67");Q0=makeQuery(id+"F3.imprint","IMPRINT",FACE,{"disambiguationData":[TD([[makeQuery(id+"F3.imprint","IMPRINT",EDGE,{"derivedFrom":subQ5}),1.0]])]});}
            var Q1;
            {var subQ5=sQuery(id+"F3.wireOp",EDGE,"E68");Q1=makeQuery(id+"F3.imprint","IMPRINT",FACE,{"disambiguationData":[TD([[makeQuery(id+"F3.imprint","IMPRINT",EDGE,{"derivedFrom":subQ5}),-1.0]])]});}
            var Q2;
            {var subQ5=sQuery(id+"F3.wireOp",EDGE,"E69");Q2=makeQuery(id+"F3.imprint","IMPRINT",FACE,{"disambiguationData":[TD([[makeQuery(id+"F3.imprint","IMPRINT",EDGE,{"derivedFrom":subQ5}),1.0]])]});}
            var Q3;
            {var subQ5=sQuery(id+"F3.wireOp",EDGE,"E70");Q3=makeQuery(id+"F3.imprint","IMPRINT",FACE,{"disambiguationData":[TD([[makeQuery(id+"F3.imprint","IMPRINT",EDGE,{"derivedFrom":subQ5}),1.0]])]});}
            extrude(context, id + "F20", {"entities" : qUnion([Q0, Q1, Q2, Q3]), "operationType" : NewBodyOperationType.ADD, "oppositeDirection" : true, "depth" : 700 * mm, "offsetDistance" : 25 * mm});
        }
        {
            var Q0;
            Q0=qCreatedBy(makeId("Front.planeOp"),FACE);
            var sketch = newSketch(context, id + "F21", { "sketchPlane" : qUnion([Q0])});
            skPoint(sketch, "E87.middle", {"position": v(0, -640) * mm});
            skPoint(sketch, "E88", {"position": v(0, -600) * mm});
            skLineSegment(sketch, "E89.bottom", {"start": v(-50, -640) * mm, "end": v(50, -640) * mm});
            skLineSegment(sketch, "E89.top", {"start": v(-50, -560) * mm, "end": v(50, -560) * mm});
            skLineSegment(sketch, "E89.left", {"start": v(-50, -640) * mm, "end": v(-50, -560) * mm});
            skLineSegment(sketch, "E89.right", {"start": v(50, -640) * mm, "end": v(50, -560) * mm});
            skSolve(sketch);
        }
        {
            var Q0;
            Q0=makeQuery(id+"F21.imprint","IMPRINT",FACE,{"disambiguationData":[TD([[makeQuery(id+"F21.imprint","IMPRINT",EDGE,{"derivedFrom":sQuery(id+"F21.wireOp",EDGE,"E89.bottom")}),1.0]])]});
            extrude(context, id + "F22", {"entities" : qUnion([Q0]), "operationType" : NewBodyOperationType.REMOVE, "oppositeDirection" : true, "depth" : 700 * mm, "offsetDistance" : 25 * mm, "symmetric" : true});
        }
        {
            var Q0;
            {var subQ0=sQuery(id+"F3.wireOp",EDGE,"E55");var subQ3=sQuery(id+"F2.wireOp",EDGE,"E19");Q0=makeQuery(id+"F20.boolean.opBoolean","MERGE",FACE,{"derivedFrom":[makeQuery(id+"F19.opExtrude","SWEPT_FACE",FACE,{"disambiguationData":[OSD([subQ3]),TDD([makeQuery(id+"F2.imprint","IMPRINT",EDGE,{"disambiguationData":[TD([[makeQuery(id+"F2.imprint","INTERSECT",VERTEX,{"derivedFrom":[subQ3,sQuery(id+"F2.wireOp",EDGE,"E27")]}),-1.0]])],"derivedFrom":subQ3}),makeQuery(id+"F2.imprint","IMPRINT",EDGE,{"disambiguationData":[TD([[makeQuery(id+"F2.imprint","INTERSECT",VERTEX,{"derivedFrom":[subQ3,sQuery(id+"F2.wireOp",EDGE,"E33")]}),1.0]])],"derivedFrom":subQ3})])]}),makeQuery(id+"F19.opExtrude","SWEPT_FACE",FACE,{"disambiguationData":[OSD([subQ3]),TDD([makeQuery(id+"F2.imprint","IMPRINT",EDGE,{"disambiguationData":[TD([[makeQuery(id+"F2.imprint","INTERSECT",VERTEX,{"derivedFrom":[subQ3,sQuery(id+"F2.wireOp",EDGE,"E34")]}),-1.0]])],"derivedFrom":subQ3}),makeQuery(id+"F2.imprint","IMPRINT",EDGE,{"disambiguationData":[TD([[makeQuery(id+"F2.imprint","INTERSECT",VERTEX,{"derivedFrom":[subQ3,sQuery(id+"F2.wireOp",EDGE,"E28")]}),1.0]])],"derivedFrom":subQ3})])]}),makeQuery(id+"F20.opExtrude","SWEPT_FACE",FACE,{"disambiguationData":[OSD([subQ0]),TDD([makeQuery(id+"F3.imprint","IMPRINT",EDGE,{"disambiguationData":[TD([[makeQuery(id+"F3.imprint","INTERSECT",VERTEX,{"derivedFrom":[subQ0,sQuery(id+"F3.wireOp",EDGE,"E67")]}),-1.0]])],"derivedFrom":subQ0}),makeQuery(id+"F3.imprint","IMPRINT",EDGE,{"disambiguationData":[TD([[makeQuery(id+"F3.imprint","INTERSECT",VERTEX,{"derivedFrom":[subQ0,sQuery(id+"F3.wireOp",EDGE,"E68")]}),1.0]])],"derivedFrom":subQ0})])]}),makeQuery(id+"F20.opExtrude","SWEPT_FACE",FACE,{"disambiguationData":[OSD([subQ0]),TDD([makeQuery(id+"F3.imprint","IMPRINT",EDGE,{"disambiguationData":[TD([[makeQuery(id+"F3.imprint","INTERSECT",VERTEX,{"derivedFrom":[subQ0,sQuery(id+"F3.wireOp",EDGE,"E69")]}),-1.0]])],"derivedFrom":subQ0}),makeQuery(id+"F3.imprint","IMPRINT",EDGE,{"disambiguationData":[TD([[makeQuery(id+"F3.imprint","INTERSECT",VERTEX,{"derivedFrom":[subQ0,sQuery(id+"F3.wireOp",EDGE,"E70")]}),1.0]])],"derivedFrom":subQ0})])]})]});}
            var sketch = newSketch(context, id + "F23", { "sketchPlane" : qUnion([Q0])});
            skPoint(sketch, "E90", {"position": v(60, 0) * mm});
            skPoint(sketch, "E90.positionSnap0", {"position": v(60, 349) * mm});
            skPoint(sketch, "E91", {"position": v(0, 60) * mm});
            skPoint(sketch, "E91.positionSnap0", {"position": v(-349, 60) * mm});
            skPoint(sketch, "E92", {"position": v(0, -60) * mm});
            skPoint(sketch, "E92.positionSnap0", {"position": v(-349, -60) * mm});
            skPoint(sketch, "E93", {"position": v(-60, 0) * mm});
            skPoint(sketch, "E93.positionSnap0", {"position": v(-60, 349) * mm});
            skSolve(sketch);
        }
        {
            var Q0;
            Q0=sQuery(id+"F23.wireOp",VERTEX,"E91");
            var Q1;
            Q1=sQuery(id+"F23.wireOp",VERTEX,"E93");
            var Q2;
            Q2=sQuery(id+"F23.wireOp",VERTEX,"E92");
            var Q3;
            Q3=sQuery(id+"F23.wireOp",VERTEX,"E90");
            var Q4;
            Q4=makeQuery(id+"F1.opExtrude","SWEPT_BODY",BODY,{"disambiguationData":[OSD([sQuery(id+"F0.wireOp",EDGE,"E0.bottom"),sQuery(id+"F0.wireOp",EDGE,"E0.top"),sQuery(id+"F0.wireOp",EDGE,"E0.left"),sQuery(id+"F0.wireOp",EDGE,"E0.right"),sQuery(id+"F0.wireOp",EDGE,"E1.bottom"),sQuery(id+"F0.wireOp",EDGE,"E1.top"),sQuery(id+"F0.wireOp",EDGE,"E1.left"),sQuery(id+"F0.wireOp",EDGE,"E1.right")])]});
            hole(context, id + "F24", {"style" : HoleStyle.SIMPLE, "endStyle" : HoleEndStyle.BLIND, "holeDiameter" : 13 * mm, "majorDiameter" : 5 * mm, "holeDepth" : 5 * mm, "isTappedThrough" : true, "tappedDepth" : 12 * mm, "tapClearance" : 3, "locations" : qUnion([Q0, Q1, Q2, Q3]), "scope" : qUnion([Q4])});
        }
    });
